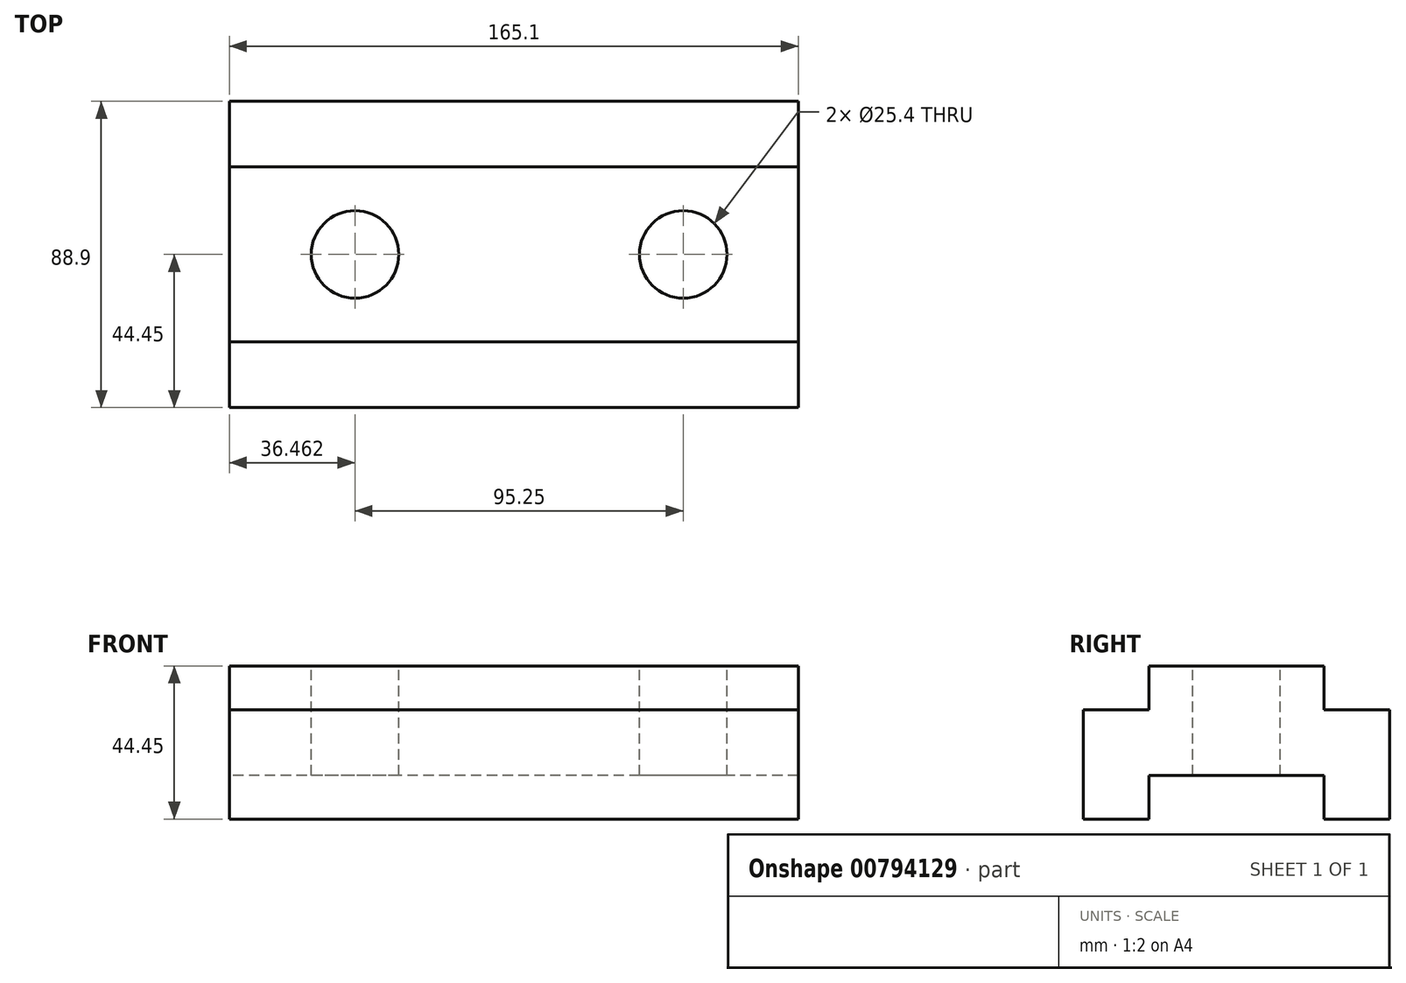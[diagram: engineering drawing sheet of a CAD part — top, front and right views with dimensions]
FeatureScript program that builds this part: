
annotation { "Feature Type Name" : "Feature", "Feature Type Description" : "" }
export const myFeature = defineFeature(function(context is Context, id is Id, definition is map)
    precondition{}
    {
        {
            var Q0;
            Q0=qCreatedBy(makeId("Right.planeOp"),FACE);
            var sketch = newSketch(context, id + "F0", { "sketchPlane" : qUnion([Q0])});
            skLineSegment(sketch, "E0", {"start": v(0, 0) * mm, "end": v(19.05, 0) * mm});
            skLineSegment(sketch, "E1", {"start": v(19.05, 0) * mm, "end": v(19.05, 12.7) * mm});
            skLineSegment(sketch, "E2", {"start": v(19.05, 12.7) * mm, "end": v(69.85, 12.7) * mm});
            skLineSegment(sketch, "E3", {"start": v(69.85, 12.7) * mm, "end": v(69.85, 0) * mm});
            skLineSegment(sketch, "E4", {"start": v(69.85, 0) * mm, "end": v(88.9, 0) * mm});
            skLineSegment(sketch, "E5", {"start": v(88.9, 0) * mm, "end": v(88.9, 31.75) * mm});
            skLineSegment(sketch, "E6", {"start": v(88.9, 31.75) * mm, "end": v(69.85, 31.75) * mm});
            skLineSegment(sketch, "E7", {"start": v(69.85, 31.75) * mm, "end": v(69.85, 44.45) * mm});
            skLineSegment(sketch, "E8", {"start": v(69.85, 44.45) * mm, "end": v(19.05, 44.45) * mm});
            skLineSegment(sketch, "E9", {"start": v(19.05, 44.45) * mm, "end": v(19.05, 31.75) * mm});
            skLineSegment(sketch, "E10", {"start": v(19.05, 31.75) * mm, "end": v(0, 31.75) * mm});
            skLineSegment(sketch, "E11", {"start": v(0, 31.75) * mm, "end": v(0, 0) * mm});
            skSolve(sketch);
        }
        {
            var Q0;
            Q0=makeQuery(id+"F0.imprint","IMPRINT",FACE,{"disambiguationData":[TD([[makeQuery(id+"F0.imprint","IMPRINT",EDGE,{"derivedFrom":sQuery(id+"F0.wireOp",EDGE,"E0")}),1.0]])]});
            extrude(context, id + "F1", {"entities" : qUnion([Q0]), "depth" : 165.1 * mm, "offsetDistance" : 25.4 * mm});
        }
        {
            var Q0;
            Q0=makeQuery(id+"F1.opExtrude","SWEPT_FACE",FACE,{"disambiguationData":[OSD([sQuery(id+"F0.wireOp",EDGE,"E8")])]});
            var sketch = newSketch(context, id + "F2", { "sketchPlane" : qUnion([Q0])});
            skLineSegment(sketch, "E12", {"start": v(0, 69.85) * mm, "end": v(0, 44.45) * mm, "construction": true});
            skLineSegment(sketch, "E13", {"start": v(0, 44.45) * mm, "end": v(36.46, 44.45) * mm, "construction": true});
            skCircle(sketch, "E14", {"center": v(36.46, 44.45) * mm, "radius": 12.7 * mm});
            skLineSegment(sketch, "E15", {"start": v(36.46, 44.45) * mm, "end": v(131.71, 44.45) * mm, "construction": true});
            skCircle(sketch, "E16", {"center": v(131.71, 44.45) * mm, "radius": 12.7 * mm});
            skSolve(sketch);
        }
        {
            var Q0;
            Q0=makeQuery(id+"F2.imprint","IMPRINT",FACE,{"disambiguationData":[TD([[makeQuery(id+"F2.imprint","IMPRINT",EDGE,{"derivedFrom":sQuery(id+"F2.wireOp",EDGE,"E14")}),1.0]])]});
            var Q1;
            Q1=makeQuery(id+"F2.imprint","IMPRINT",FACE,{"disambiguationData":[TD([[makeQuery(id+"F2.imprint","IMPRINT",EDGE,{"derivedFrom":sQuery(id+"F2.wireOp",EDGE,"E16")}),1.0]])]});
            extrude(context, id + "F3", {"entities" : qUnion([Q0, Q1]), "operationType" : NewBodyOperationType.REMOVE, "endBound" : BoundingType.THROUGH_ALL, "oppositeDirection" : true, "depth" : 25.4 * mm, "offsetDistance" : 25.4 * mm});
        }
    });
